# Revit family: Haworth_BeHold_OverheadStorage_HingedDoor
name_source: partatom
category: Furniture Systems
revit_build: Autodesk Revit 2018 (Build: 20170223_1515(x64)
units: mm (PartAtom-declared; Revit-internal decimal feet)

## family parameters
Always vertical = Yes
Cut with Voids When Loaded = No
OmniClass Number = 23.40.70.14.64.21
OmniClass Title = Systems Furniture
Part Type = Normal
Room Calculation Point = No
Round Connector Dimension = Use Diameter
Shared = No
Work Plane-Based = No

## types (9) — shared parameters
Actual Depth = 15.94 "
Actual Height = 16 "
Assembly Code = E2020200
Back Finish = Haworth _ Laminate _ Beige H-34
Cabinet Finish = Haworth _ Laminate _ Beige H-34
Door Height = 14.57 "
Manufacturer = Haworth
Max. Width = 72 "
Min. Width = 24 "
Model = Haworth Be_Hold
Mounting Height = 22 "
Revision Number = 1
Size = Verify Final Dim. w/ Haworth
Standard Widths = 24 - 72in @ 6in increments
Sustainability Info = https://www.haworth.com
Two Doors = Yes
URL = www.haworth.com
URL - Product = https://www.haworth.com
Warranty = http://www.haworth.com

## per-type parameters (varying)
| type | Actual Width | Custom Size | Description | Door Width | Four Doors | Width |
| 16h 36w | 36 " | No | Haworth - Be_Hold - Overhead Storage Unit - Hinged Door - 16h 36w | 18 " | No | 36 " |
| 16h 24w | 24 " | Yes | Haworth - Be_Hold - Overhead Storage Unit - Hinged Door - 16h 36w | 12 " | No | 24 " |
| 16h 30w | 30 " | Yes | Haworth - Be_Hold - Overhead Storage Unit - Hinged Door - 16h 36w | 15 " | No | 30 " |
| 16h 42w | 42 " | No | Haworth - Be_Hold - Overhead Storage Unit - Hinged Door - 16h 36w | 10.5 " | Yes | 42 " |
| 16h 48w | 48 " | No | Haworth - Be_Hold - Overhead Storage Unit - Hinged Door - 16h 36w | 12 " | Yes | 48 " |
| 16h 54w | 54 " | No | Haworth - Be_Hold - Overhead Storage Unit - Hinged Door - 16h 36w | 13.5 " | Yes | 54 " |
| 16h 72w | 72 " | No | Haworth - Be_Hold - Overhead Storage Unit - Hinged Door - 16h 72w | 18 " | Yes | 72 " |
| 16h 66w | 66 " | No | Haworth - Be_Hold - Overhead Storage Unit - Hinged Door - 16h 36w | 16.5 " | Yes | 66 " |
| 16h 60w | 60 " | No | Haworth - Be_Hold - Overhead Storage Unit - Hinged Door - 16h 36w | 15 " | Yes | 60 " |

## geometry (parser evidence)
native form markers: Sweep x9
no freeform markers — native parametric forms only
